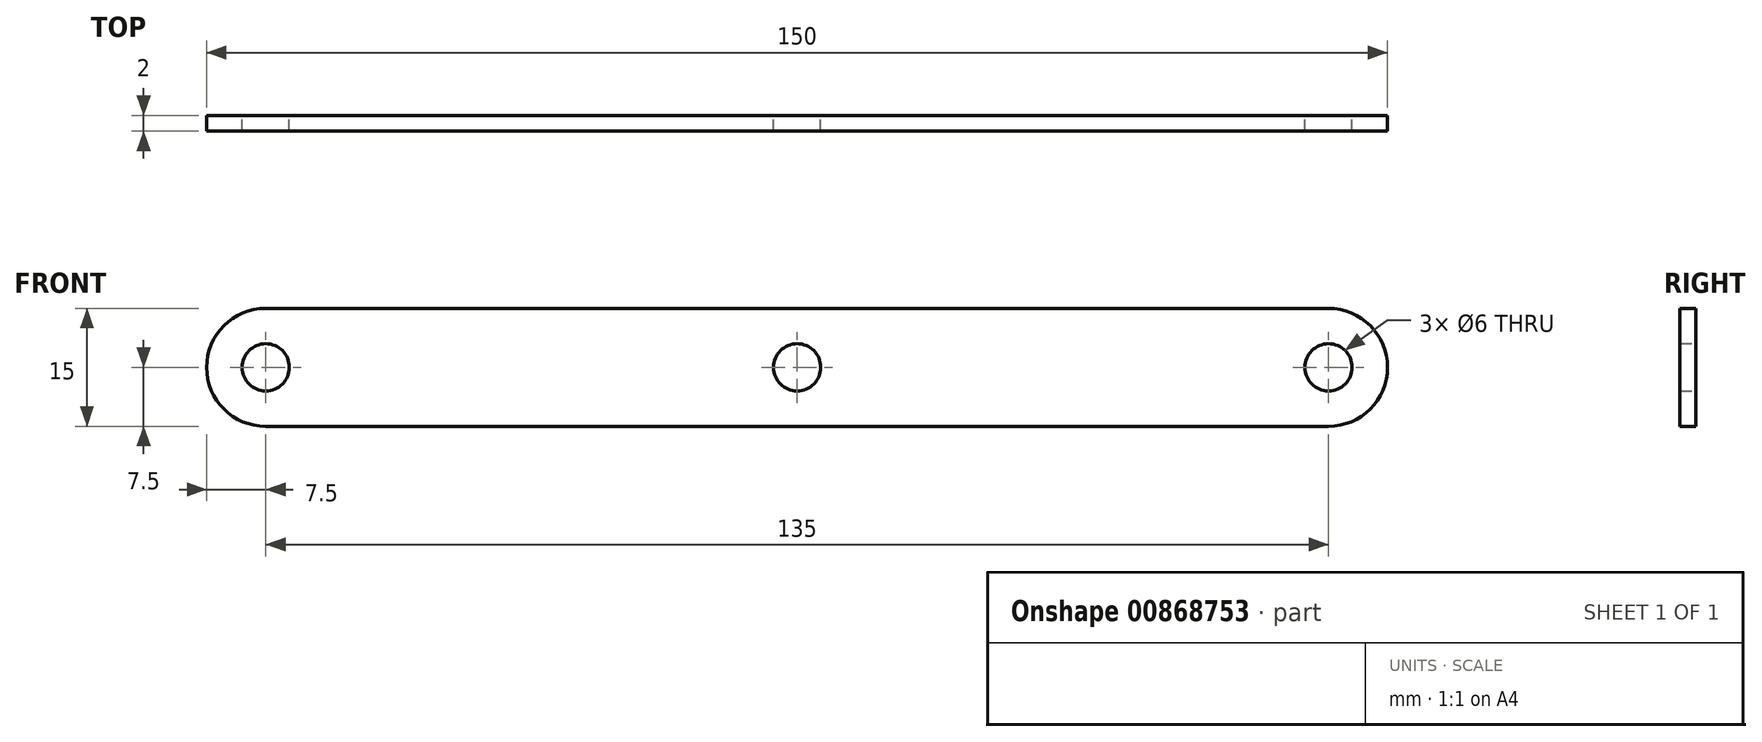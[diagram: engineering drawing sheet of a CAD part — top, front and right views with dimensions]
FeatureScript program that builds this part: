
annotation { "Feature Type Name" : "Feature", "Feature Type Description" : "" }
export const myFeature = defineFeature(function(context is Context, id is Id, definition is map)
    precondition{}
    {
        {
            var Q0;
            Q0=qCreatedBy(makeId("Front.planeOp"),FACE);
            var sketch = newSketch(context, id + "F0", { "sketchPlane" : qUnion([Q0])});
            skCircle(sketch, "E0", {"center": v(0, 0) * mm, "radius": 3 * mm});
            skLineSegment(sketch, "E1.bottom", {"start": v(-7.5, -7.5) * mm, "end": v(142.5, -7.5) * mm});
            skLineSegment(sketch, "E1.top", {"start": v(-7.5, 7.5) * mm, "end": v(142.5, 7.5) * mm});
            skLineSegment(sketch, "E1.left", {"start": v(-7.5, -7.5) * mm, "end": v(-7.5, 7.5) * mm});
            skLineSegment(sketch, "E1.right", {"start": v(142.5, -7.5) * mm, "end": v(142.5, 7.5) * mm});
            skCircle(sketch, "E2", {"center": v(135, 0) * mm, "radius": 3 * mm});
            skCircle(sketch, "E3", {"center": v(67.5, 0) * mm, "radius": 3 * mm});
            skSolve(sketch);
        }
        {
            var Q0;
            Q0=makeQuery(id+"F0.imprint","IMPRINT",FACE,{"disambiguationData":[TD([[makeQuery(id+"F0.imprint","IMPRINT",EDGE,{"derivedFrom":sQuery(id+"F0.wireOp",EDGE,"E0")}),-1.0]])]});
            extrude(context, id + "F1", {"entities" : qUnion([Q0]), "depth" : 2 * mm, "offsetDistance" : 25 * mm, "symmetric" : true});
        }
        {
            var Q0;
            Q0=makeQuery(id+"F1.opExtrude","SWEPT_EDGE",EDGE,{"disambiguationData":[OSD([sQuery(id+"F0.wireOp",EDGE,"E1.top"),sQuery(id+"F0.wireOp",EDGE,"E1.right")])]});
            var Q1;
            Q1=makeQuery(id+"F1.opExtrude","SWEPT_EDGE",EDGE,{"disambiguationData":[OSD([sQuery(id+"F0.wireOp",EDGE,"E1.bottom"),sQuery(id+"F0.wireOp",EDGE,"E1.right")])]});
            var Q2;
            Q2=makeQuery(id+"F1.opExtrude","SWEPT_EDGE",EDGE,{"disambiguationData":[OSD([sQuery(id+"F0.wireOp",EDGE,"E1.top"),sQuery(id+"F0.wireOp",EDGE,"E1.left")])]});
            var Q3;
            Q3=makeQuery(id+"F1.opExtrude","SWEPT_EDGE",EDGE,{"disambiguationData":[OSD([sQuery(id+"F0.wireOp",EDGE,"E1.bottom"),sQuery(id+"F0.wireOp",EDGE,"E1.left")])]});
            fillet(context, id + "F2", {"entities" : qUnion([Q0, Q1, Q2, Q3]), "radius" : 7.5 * mm, "tangentPropagation" : true, "allowEdgeOverflow" : false});
        }
    });
